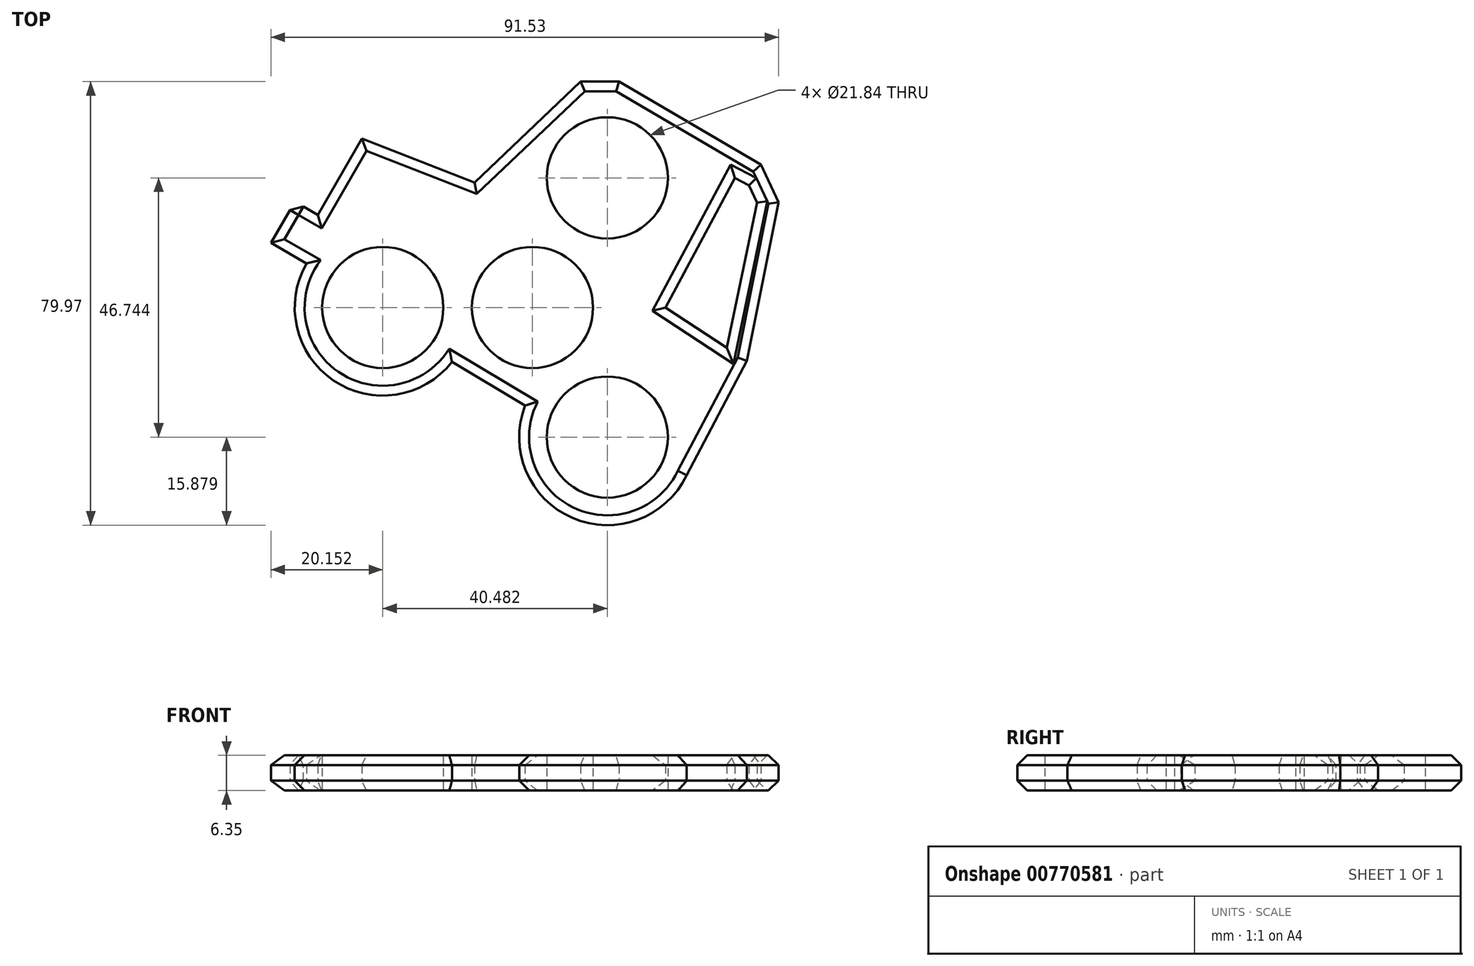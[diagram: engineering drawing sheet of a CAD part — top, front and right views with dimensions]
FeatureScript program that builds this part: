
annotation { "Feature Type Name" : "Feature", "Feature Type Description" : "" }
export const myFeature = defineFeature(function(context is Context, id is Id, definition is map)
    precondition{}
    {
        {
            var Q0;
            Q0=qCreatedBy(makeId("Top.planeOp"),FACE);
            var sketch = newSketch(context, id + "F0", { "sketchPlane" : qUnion([Q0])});
            skLineSegment(sketch, "E0", {"start": v(-15.88, 0) * mm, "end": v(-11.11, 0) * mm});
            skLineSegment(sketch, "E1", {"start": v(-11.11, 0) * mm, "end": v(-26.99, 0) * mm});
            skCircle(sketch, "E2", {"center": v(-26.99, 0) * mm, "radius": 15.88 * mm});
            skCircle(sketch, "E3.1.0", {"center": v(13.5, -23.37) * mm, "radius": 15.88 * mm});
            skPoint(sketch, "E3.center", {"position": v(0, 0) * mm});
            skLineSegment(sketch, "E4", {"start": v(-47.14, 11.64) * mm, "end": v(-42.84, 19.1) * mm});
            skLineSegment(sketch, "E5", {"start": v(-42.84, 19.1) * mm, "end": v(-38.67, 16.69) * mm});
            skLineSegment(sketch, "E6", {"start": v(-38.67, 16.69) * mm, "end": v(-30.73, 30.44) * mm});
            skLineSegment(sketch, "E7", {"start": v(-30.73, 30.44) * mm, "end": v(-10.43, 22.55) * mm});
            skLineSegment(sketch, "E8", {"start": v(38.68, -9.63) * mm, "end": v(27.24, -31.3) * mm});
            skLineSegment(sketch, "E9", {"start": v(-47.14, 11.64) * mm, "end": v(-40.74, 7.94) * mm});
            skLineSegment(sketch, "E10", {"start": v(41.16, 25.75) * mm, "end": v(44.39, 18.96) * mm});
            skLineSegment(sketch, "E11", {"start": v(44.39, 18.96) * mm, "end": v(38.68, -9.63) * mm});
            skLineSegment(sketch, "E12", {"start": v(-14.51, -9.82) * mm, "end": v(-1.33, -17.7) * mm});
            skPoint(sketch, "E13", {"position": v(13.5, 23.37) * mm});
            skPoint(sketch, "E14.startSnap0", {"position": v(36.8, 6.35) * mm});
            skLineSegment(sketch, "E15", {"start": v(40.48, 18.92) * mm, "end": v(39, 22.03) * mm});
            skLineSegment(sketch, "E16", {"start": v(39, 22.03) * mm, "end": v(36.48, 23.36) * mm});
            skLineSegment(sketch, "E17", {"start": v(36.48, 23.36) * mm, "end": v(23.99, 0) * mm});
            skLineSegment(sketch, "E18", {"start": v(40.48, 18.92) * mm, "end": v(35.05, -7.25) * mm});
            skLineSegment(sketch, "E19", {"start": v(35.05, -7.25) * mm, "end": v(23.99, 0) * mm});
            skLineSegment(sketch, "E20", {"start": v(15.58, 40.72) * mm, "end": v(8.7, 40.72) * mm});
            skLineSegment(sketch, "E21", {"start": v(41.16, 25.75) * mm, "end": v(15.58, 40.72) * mm});
            skLineSegment(sketch, "E22", {"start": v(8.7, 40.72) * mm, "end": v(-10.43, 22.55) * mm});
            skLineSegment(sketch, "E23", {"start": v(13.5, -23.37) * mm, "end": v(27.24, -31.3) * mm});
            skLineSegment(sketch, "E24", {"start": v(13.5, -23.37) * mm, "end": v(0, -15.58) * mm});
            skSolve(sketch);
        }
        {
            var Q0;
            Q0 = qSketchRegion(id + "F0", true);
            extrude(context, id + "F1", {"entities" : qUnion([Q0]), "depth" : 6.35 * mm, "offsetDistance" : 25.4 * mm});
        }
        {
            var Q0;
            Q0=sQuery(id+"F0.wireOp",VERTEX,"E13");
            var Q1;
            Q1=sQuery(id+"F0.wireOp",VERTEX,"E3.center");
            var Q2;
            Q2=sQuery(id+"F0.wireOp",VERTEX,"E3.1.0.center");
            var Q3;
            Q3=sQuery(id+"F0.wireOp",VERTEX,"E2.center");
            var Q4;
            Q4=makeQuery(id+"F1.opExtrude","SWEPT_BODY",BODY,{"disambiguationData":[OSD([sQuery(id+"F0.wireOp",EDGE,"E2"),sQuery(id+"F0.wireOp",EDGE,"E3.1.0"),sQuery(id+"F0.wireOp",EDGE,"E4"),sQuery(id+"F0.wireOp",EDGE,"E5"),sQuery(id+"F0.wireOp",EDGE,"E6"),sQuery(id+"F0.wireOp",EDGE,"E7"),sQuery(id+"F0.wireOp",EDGE,"g700lsHG-AgUQ-3GBr-k54n-3yH2lDKWjnYI"),sQuery(id+"F0.wireOp",EDGE,"E8"),sQuery(id+"F0.wireOp",EDGE,"E9"),sQuery(id+"F0.wireOp",EDGE,"E10"),sQuery(id+"F0.wireOp",EDGE,"nqbn0w8B-B6vS-X88F-MwCJ-TpIs3RYWCSOC"),sQuery(id+"F0.wireOp",EDGE,"E11"),sQuery(id+"F0.wireOp",EDGE,"E12")])]});
            hole(context, id + "F2", {"style" : HoleStyle.SIMPLE, "endStyle" : HoleEndStyle.THROUGH, "oppositeDirection" : true, "holeDiameter" : 21.84 * mm, "majorDiameter" : 6.35 * mm, "isTappedThrough" : true, "tappedDepth" : 12.7 * mm, "tapClearance" : 3, "locations" : qUnion([Q0, Q1, Q2, Q3]), "scope" : qUnion([Q4])});
        }
        {
            var Q0;
            Q0=makeQuery(id+"F1.opExtrude","CAP_EDGE",EDGE,{"disambiguationData":[OSD([sQuery(id+"F0.wireOp",EDGE,"E22")])],"isStart":true});
            var Q1;
            Q1=makeQuery(id+"F1.opExtrude","CAP_EDGE",EDGE,{"disambiguationData":[OSD([sQuery(id+"F0.wireOp",EDGE,"E22")])],"isStart":false});
            var Q2;
            Q2=makeQuery(id+"F1.opExtrude","CAP_EDGE",EDGE,{"disambiguationData":[OSD([sQuery(id+"F0.wireOp",EDGE,"E7")])],"isStart":true});
            var Q3;
            Q3=makeQuery(id+"F1.opExtrude","CAP_EDGE",EDGE,{"disambiguationData":[OSD([sQuery(id+"F0.wireOp",EDGE,"E7")])],"isStart":false});
            var Q4;
            Q4=makeQuery(id+"F1.opExtrude","CAP_EDGE",EDGE,{"disambiguationData":[OSD([sQuery(id+"F0.wireOp",EDGE,"E6")])],"isStart":true});
            var Q5;
            Q5=makeQuery(id+"F1.opExtrude","CAP_EDGE",EDGE,{"disambiguationData":[OSD([sQuery(id+"F0.wireOp",EDGE,"E6")])],"isStart":false});
            var Q6;
            Q6=makeQuery(id+"F1.opExtrude","CAP_EDGE",EDGE,{"disambiguationData":[OSD([sQuery(id+"F0.wireOp",EDGE,"E5")])],"isStart":true});
            var Q7;
            Q7=makeQuery(id+"F1.opExtrude","SWEPT_EDGE",EDGE,{"disambiguationData":[OSD([sQuery(id+"F0.wireOp",EDGE,"E4"),sQuery(id+"F0.wireOp",EDGE,"E5")])]});
            var Q8;
            Q8=makeQuery(id+"F1.opExtrude","CAP_EDGE",EDGE,{"disambiguationData":[OSD([sQuery(id+"F0.wireOp",EDGE,"E5")])],"isStart":false});
            var Q9;
            Q9=makeQuery(id+"F1.opExtrude","CAP_EDGE",EDGE,{"disambiguationData":[OSD([sQuery(id+"F0.wireOp",EDGE,"E4")])],"isStart":false});
            var Q10;
            Q10=makeQuery(id+"F1.opExtrude","CAP_EDGE",EDGE,{"disambiguationData":[OSD([sQuery(id+"F0.wireOp",EDGE,"E4")])],"isStart":true});
            var Q11;
            Q11=makeQuery(id+"F1.opExtrude","CAP_EDGE",EDGE,{"disambiguationData":[OSD([sQuery(id+"F0.wireOp",EDGE,"E9")])],"isStart":true});
            var Q12;
            Q12=makeQuery(id+"F1.opExtrude","CAP_EDGE",EDGE,{"disambiguationData":[OSD([sQuery(id+"F0.wireOp",EDGE,"E9")])],"isStart":false});
            var Q13;
            Q13=makeQuery(id+"F1.opExtrude","CAP_EDGE",EDGE,{"disambiguationData":[OSD([sQuery(id+"F0.wireOp",EDGE,"E2")])],"isStart":true});
            var Q14;
            Q14=makeQuery(id+"F1.opExtrude","CAP_EDGE",EDGE,{"disambiguationData":[OSD([sQuery(id+"F0.wireOp",EDGE,"E2")])],"isStart":false});
            var Q15;
            Q15=makeQuery(id+"F1.opExtrude","CAP_EDGE",EDGE,{"disambiguationData":[OSD([sQuery(id+"F0.wireOp",EDGE,"E12")])],"isStart":true});
            var Q16;
            Q16=makeQuery(id+"F1.opExtrude","CAP_EDGE",EDGE,{"disambiguationData":[OSD([sQuery(id+"F0.wireOp",EDGE,"E12")])],"isStart":false});
            var Q17;
            Q17=makeQuery(id+"F1.opExtrude","CAP_EDGE",EDGE,{"disambiguationData":[OSD([sQuery(id+"F0.wireOp",EDGE,"E3.1.0")])],"isStart":true});
            var Q18;
            Q18=makeQuery(id+"F1.opExtrude","CAP_EDGE",EDGE,{"disambiguationData":[OSD([sQuery(id+"F0.wireOp",EDGE,"E3.1.0")])],"isStart":false});
            var Q19;
            Q19=makeQuery(id+"F1.opExtrude","CAP_EDGE",EDGE,{"disambiguationData":[OSD([sQuery(id+"F0.wireOp",EDGE,"E11")])],"isStart":true});
            var Q20;
            Q20=makeQuery(id+"F1.opExtrude","CAP_EDGE",EDGE,{"disambiguationData":[OSD([sQuery(id+"F0.wireOp",EDGE,"E11")])],"isStart":false});
            var Q21;
            Q21=makeQuery(id+"F1.opExtrude","CAP_EDGE",EDGE,{"disambiguationData":[OSD([sQuery(id+"F0.wireOp",EDGE,"E10")])],"isStart":true});
            var Q22;
            Q22=makeQuery(id+"F1.opExtrude","CAP_EDGE",EDGE,{"disambiguationData":[OSD([sQuery(id+"F0.wireOp",EDGE,"E10")])],"isStart":false});
            var Q23;
            Q23=makeQuery(id+"F1.opExtrude","CAP_EDGE",EDGE,{"disambiguationData":[OSD([sQuery(id+"F0.wireOp",EDGE,"E20")])],"isStart":true});
            var Q24;
            Q24=makeQuery(id+"F1.opExtrude","CAP_EDGE",EDGE,{"disambiguationData":[OSD([sQuery(id+"F0.wireOp",EDGE,"E20")])],"isStart":false});
            var Q25;
            Q25=makeQuery(id+"F1.opExtrude","CAP_EDGE",EDGE,{"disambiguationData":[OSD([sQuery(id+"F0.wireOp",EDGE,"E21")])],"isStart":true});
            var Q26;
            Q26=makeQuery(id+"F1.opExtrude","CAP_EDGE",EDGE,{"disambiguationData":[OSD([sQuery(id+"F0.wireOp",EDGE,"E21")])],"isStart":false});
            var Q27;
            Q27=makeQuery(id+"F1.opExtrude","CAP_EDGE",EDGE,{"disambiguationData":[OSD([sQuery(id+"F0.wireOp",EDGE,"E19")])],"isStart":true});
            var Q28;
            Q28=makeQuery(id+"F1.opExtrude","CAP_EDGE",EDGE,{"disambiguationData":[OSD([sQuery(id+"F0.wireOp",EDGE,"E17")])],"isStart":true});
            var Q29;
            Q29=makeQuery(id+"F1.opExtrude","CAP_EDGE",EDGE,{"disambiguationData":[OSD([sQuery(id+"F0.wireOp",EDGE,"E18")])],"isStart":true});
            var Q30;
            Q30=makeQuery(id+"F1.opExtrude","CAP_EDGE",EDGE,{"disambiguationData":[OSD([sQuery(id+"F0.wireOp",EDGE,"E16")])],"isStart":true});
            var Q31;
            Q31=makeQuery(id+"F1.opExtrude","CAP_EDGE",EDGE,{"disambiguationData":[OSD([sQuery(id+"F0.wireOp",EDGE,"E15")])],"isStart":true});
            var Q32;
            Q32=makeQuery(id+"F1.opExtrude","CAP_EDGE",EDGE,{"disambiguationData":[OSD([sQuery(id+"F0.wireOp",EDGE,"E16")])],"isStart":false});
            var Q33;
            Q33=makeQuery(id+"F1.opExtrude","CAP_EDGE",EDGE,{"disambiguationData":[OSD([sQuery(id+"F0.wireOp",EDGE,"E17")])],"isStart":false});
            var Q34;
            Q34=makeQuery(id+"F1.opExtrude","CAP_EDGE",EDGE,{"disambiguationData":[OSD([sQuery(id+"F0.wireOp",EDGE,"E18")])],"isStart":false});
            var Q35;
            Q35=makeQuery(id+"F1.opExtrude","CAP_EDGE",EDGE,{"disambiguationData":[OSD([sQuery(id+"F0.wireOp",EDGE,"E15")])],"isStart":false});
            var Q36;
            Q36=makeQuery(id+"F1.opExtrude","CAP_EDGE",EDGE,{"disambiguationData":[OSD([sQuery(id+"F0.wireOp",EDGE,"E19")])],"isStart":false});
            chamfer(context, id + "F3", {"entities" : qUnion([Q0, Q1, Q2, Q3, Q4, Q5, Q6, Q7, Q8, Q9, Q10, Q11, Q12, Q13, Q14, Q15, Q16, Q17, Q18, Q19, Q20, Q21, Q22, Q23, Q24, Q25, Q26, Q27, Q28, Q29, Q30, Q31, Q32, Q33, Q34, Q35, Q36]), "width" : 1.78 * mm, "tangentPropagation" : true});
        }
    });
